# Revit family: РОСМА_МанометрСтандартногоИсполнения_М2
name_source: partatom
category: Арматура трубопроводов
revit_build: Autodesk Revit 2018 (Build: 20180423_1000(x64)
units: mm (PartAtom-declared; Revit-internal decimal feet)

## family parameters
Всегда вертикально = Да
На основе рабочей плоскости = Нет
Общий = Нет
При загрузке вырезать с полостями = Нет
Размер круглого соединителя = Использовать диаметр
Тип детали = Вставляется

## types (1)
- ТМ-510Р
    ADSK_Единица измерения = шт.
    ADSK_Количество = 1
    D = 100 мм
    D1 = 100 мм
    D2 = 98 мм
    DN = 15.00 мм
    Dполости_переднСт = 92 мм
    G = 20 мм
    Lgol = 2 мм
    Lrezba = 15 мм
    R1_шкала = 41 мм
    R2_шкала = 40 мм
    R_лого = 0 мм
    S = 14 мм
    Table = спец_10серия_М2
    URL = https://rosma.spb.ru
    b = 34 мм
    e = 20 мм
    f = 11 мм
    h = 74 мм
    h гайки = 10 мм
    Группа модели = Оборудование
    Давление01 = ‎ : ТМ 0…0,25МПа
    Давление02 = ‎ : ТМ 0…0,4МПа
    Давление03 = ‎ : ТМ 0…0,6МПа
    Давление04 = ‎ : ТМ 0…1,0МПа
    Давление05 = ‎ : ТМ 0…1,6МПа
    Давление06 = ‎ : ТМ 0…2,5МПа
    Давление07 = ‎ : ТМ 0…4МПа
    Давление08 = ‎ : ТМ 0…6МПа
    Диапазон раб. температур измер. среды = от -50°С до +150°С
    Диапазон раб. температур окр. среды = от -60°С до +60°С
    Изготовитель = ЗАО "РОСМА"
    Класс точности = 1.5
    Климатическое исполнение = Группа В3; климат. исполн. УХЛ кат. 3.1
    Код IP = IP40
    Межповерочный интервал = 2 года
    Описание = Манометр показывающий ТМ серия 10, модель 2,  стандартного исполнения с облегченным штуцером, рекомендована для объектов ЖКХ
    Присоединение = Радиальное
    Таблица поиска = Манометр стандартного исполнения М2
    Техническая документация = ТУ 4212-001-4719015564-2008; ГОСТ 2405–88
